# Revit family: v-316_317k7_kr7_kp7_50Hz - コピー
name_source: partatom
category: 機械設備
units: mm (PartAtom-declared; Revit-internal decimal feet)

## family parameters
OmniClass タイトル = Centrifugal Fans
OmniClass 番号 = 23.75.35.17.27
パーツ タイプ = 標準
ロード時にボイドで切り取り = いいえ
丸型コネクタ寸法 = 直径を使用
作業面ベース = いいえ
共有 = いいえ
常に垂直 = はい
部屋計算ポイント = いいえ

## types (1)
- V-316KSW6
    Box_D = 235  [stored 0.770997 ft]
    Box_Depth = 80  [stored 0.262467 ft]
    Box_Height = 22  [stored 0.0721785 ft]
    Box_Width = 85  [stored 0.278871 ft]
    Clearance Back = 0  [stored 0 ft]
    Clearance Bottom = 0  [stored 0 ft]
    Clearance Front = 0  [stored 0 ft]
    Clearance Left = 0  [stored 0 ft]
    Clearance Right = 0  [stored 0 ft]
    Clearance Top = 0  [stored 0 ft]
    D1 = 95
    Depth = 580  [stored 1.90289 ft]
    Duct_D = 178  [stored 0.58399 ft]
    Duct_H = 91  [stored 0.298556 ft]
    Duct_Height = 46  [stored 0.150919 ft]
    Duct_W = 210  [stored 0.688976 ft]
    EAサイズ_D = 291  [stored 0.954724 ft]
    EAサイズ_W = 102
    EAダクト接続口_上部右 = はい
    EAダクト接続口_上部左 = いいえ
    EAダクト接続口_右 = いいえ
    EAダクト接続口_左 = いいえ
    EAダクト接続口_後部 = いいえ
    H1 = 110  [stored 0.360892 ft]
    Height = 190
    IfcExportAs = IfcFanType
    IfcExportType = CENTRIFUGALFORWARDCURVED
    MAX静圧 = 0.0 Pa
    MAX風量 = 590.0 m³/h
    MID静圧 = 0.0 Pa
    MID風量 = 0.0 m³/h
    MIN静圧 = 0.0 Pa
    MIN風量 = 360.0 m³/h
    OmniClassCode = 23-33 31 19 13 15
    URL = https://www.mitsubishielectric.co.jp
    Uniclass2015Code = Pr_65_67_29_12
    Uniclass2015Title = Centrifugal fans
    Uniclass2015Version = Systems v1.9
    W1 = 300  [stored 0.984252 ft]
    Width = 600  [stored 1.9685 ft]
    ☑給気／□排気 = いいえ
    ダクト幅 = 102 mm
    ダクト高 = 291 mm
    マテリアル = 鋼板(白)
    モデル = V-316KSW6
    仕様書バージョン = Version1.0
    企業コード = 108420
    価格 = 68100 $
    分類コード = 50052503100060
    取付金具_Depth = 6  [stored 0.019685 ft]
    取付金具_H = 30  [stored 0.0984252 ft]
    取付金具_ピッチ = 500  [stored 1.64042 ft]
    取付金具_径 = 10  [stored 0.0328084 ft]
    取付金具_穴位置 = 16  [stored 0.0524934 ft]
    周波数 = 50 Hz
    呼称 = 遠心送風機
    外気量 = 0.0 m³/h
    天吊用穴_D1 = 15  [stored 0.0492126 ft]
    天吊用穴_D2 = 336  [stored 1.10236 ft]
    天吊用穴_ピッチ = 250  [stored 0.82021 ft]
    実風量 = 0.0 m³/h
    形式 = 片吸込形
    排気量 = 0.0 m³/h
    極数 = 2
    機外静圧 = 0.0 Pa
    機外静圧_排気 = 210.0 Pa
    法定耐用年数 = 15
    消費電力 = 72 W
    相 = 1
    積算_科目 = 2 換気設備
    符号 = FE
    製品リリース年月 = 2022年6月1日
    製品出荷対象 = 国内
    製品質量 = 12.00 kg
    製造元 = 三菱電機株式会社
    設置方法 = 天吊
    設計風量 = 0.0 m³/h
    説明 = レンジフードファン 浅形 標準タイプ
    負荷分類 = 3_ファン類
    質量 = 14.40 kg
    運転質量 = 0.00 kg
    電動機出力 = 0 W
    電圧 = 100 V
    風量 = 590.0 m³/h
    騒音レベル(dB(A)) = 46.5

note: [stored X ft] marks values corroborated as IEEE doubles in the binary element streams (Revit-internal decimal feet)

## geometry (parser evidence)
native form markers: Blend x2
no freeform markers — native parametric forms only
